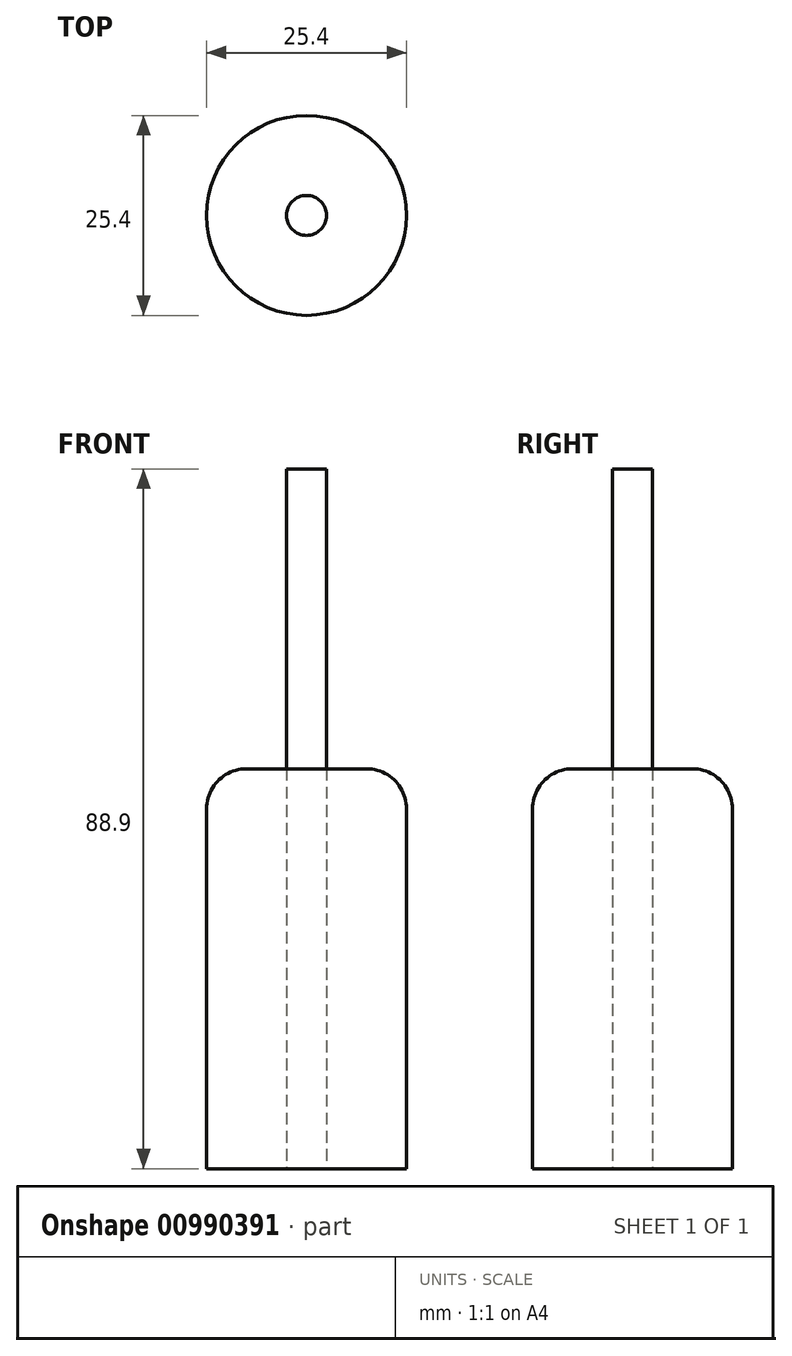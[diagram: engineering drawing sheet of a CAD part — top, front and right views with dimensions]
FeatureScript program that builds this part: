
annotation { "Feature Type Name" : "Feature", "Feature Type Description" : "" }
export const myFeature = defineFeature(function(context is Context, id is Id, definition is map)
    precondition{}
    {
        {
            var Q0;
            Q0=qCreatedBy(makeId("Top.planeOp"),FACE);
            var sketch = newSketch(context, id + "F0", { "sketchPlane" : qUnion([Q0])});
            skCircle(sketch, "E0", {"center": v(0, 0) * mm, "radius": 12.7 * mm});
            skSolve(sketch);
        }
        {
            var Q0;
            Q0 = qSketchRegion(id + "F0", true);
            extrude(context, id + "F1", {"entities" : qUnion([Q0]), "depth" : 50.8 * mm, "offsetDistance" : 25.4 * mm});
        }
        {
            var Q0;
            Q0=qCreatedBy(makeId("Top.planeOp"),FACE);
            var sketch = newSketch(context, id + "F2", { "sketchPlane" : qUnion([Q0])});
            skCircle(sketch, "E1", {"center": v(0, 0) * mm, "radius": 2.54 * mm});
            skSolve(sketch);
        }
        {
            var Q0;
            Q0=makeQuery(id+"F2.imprint","IMPRINT",FACE,{"disambiguationData":[TD([[makeQuery(id+"F2.imprint","IMPRINT",EDGE,{"derivedFrom":sQuery(id+"F2.wireOp",EDGE,"E1")}),1.0]])]});
            var Q1;
            Q1=sQuery(id+"F2.wireOp",EDGE,"E1");
            extrude(context, id + "F3", {"entities" : qUnion([Q0]), "surfaceEntities" : qUnion([Q1]), "depth" : 88.9 * mm, "offsetDistance" : 25.4 * mm});
        }
        {
            var Q0;
            Q0=makeQuery(id+"F1.opExtrude","CAP_EDGE",EDGE,{"disambiguationData":[OSD([sQuery(id+"F0.wireOp",EDGE,"E0")])],"isStart":false});
            fillet(context, id + "F4", {"entities" : qUnion([Q0]), "radius" : 5.08 * mm, "tangentPropagation" : true, "allowEdgeOverflow" : false});
        }
    });
